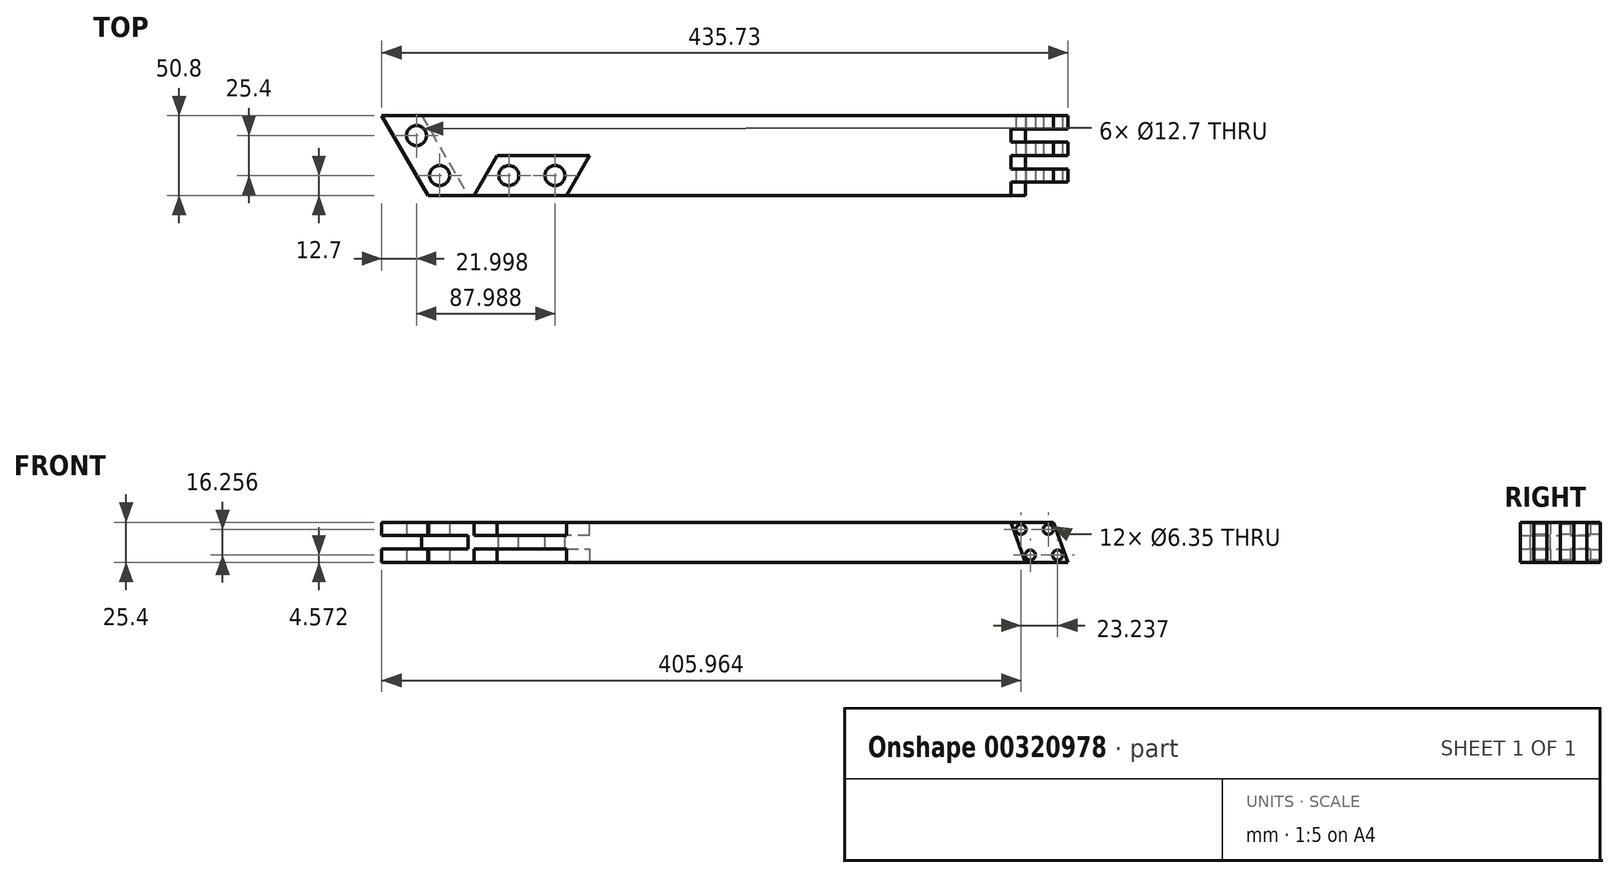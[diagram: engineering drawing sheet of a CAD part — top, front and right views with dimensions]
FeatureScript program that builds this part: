
annotation { "Feature Type Name" : "Feature", "Feature Type Description" : "" }
export const myFeature = defineFeature(function(context is Context, id is Id, definition is map)
    precondition{}
    {
        {
            var Q0;
            Q0=qCreatedBy(makeId("Top.planeOp"),FACE);
            var sketch = newSketch(context, id + "F0", { "sketchPlane" : qUnion([Q0])});
            skLineSegment(sketch, "E0", {"start": v(-203.2, -25.4) * mm, "end": v(-232.53, 25.4) * mm});
            skLineSegment(sketch, "E1", {"start": v(-232.53, 25.4) * mm, "end": v(203.2, 25.4) * mm});
            skLineSegment(sketch, "E2", {"start": v(203.2, 25.4) * mm, "end": v(203.2, -25.4) * mm});
            skLineSegment(sketch, "E3", {"start": v(203.2, -25.4) * mm, "end": v(-203.2, -25.4) * mm});
            skSolve(sketch);
        }
        {
            var Q0;
            Q0=makeQuery(id+"F0.imprint","IMPRINT",FACE,{"disambiguationData":[TD([[makeQuery(id+"F0.imprint","IMPRINT",EDGE,{"derivedFrom":sQuery(id+"F0.wireOp",EDGE,"E0")}),-1.0]])]});
            extrude(context, id + "F1", {"entities" : qUnion([Q0]), "depth" : 25.4 * mm});
        }
        {
            var Q0;
            Q0=makeQuery(id+"F1.opExtrude","CAP_FACE",FACE,{"disambiguationData":[OSD([sQuery(id+"F0.wireOp",EDGE,"E0"),sQuery(id+"F0.wireOp",EDGE,"E1"),sQuery(id+"F0.wireOp",EDGE,"E2"),sQuery(id+"F0.wireOp",EDGE,"E3")])],"isStart":false});
            var sketch = newSketch(context, id + "F2", { "sketchPlane" : qUnion([Q0])});
            skLineSegment(sketch, "E4", {"start": v(-173.87, -25.4) * mm, "end": v(-159.2, 0) * mm});
            skLineSegment(sketch, "E5", {"start": v(-159.2, 0) * mm, "end": v(-100.55, 0) * mm});
            skLineSegment(sketch, "E6", {"start": v(-100.55, 0) * mm, "end": v(-115.21, -25.4) * mm});
            skLineSegment(sketch, "E7", {"start": v(-115.21, -25.4) * mm, "end": v(-173.87, -25.4) * mm});
            skLineSegment(sketch, "E8", {"start": v(-203.2, 25.4) * mm, "end": v(-173.87, -25.4) * mm, "construction": true});
            skSolve(sketch);
        }
        {
            var Q0;
            Q0=makeQuery(id+"F2.imprint","IMPRINT",FACE,{"disambiguationData":[TD([[makeQuery(id+"F2.imprint","IMPRINT",EDGE,{"derivedFrom":sQuery(id+"F2.wireOp",EDGE,"E4")}),-1.0]])]});
            extrude(context, id + "F3", {"entities" : qUnion([Q0]), "operationType" : NewBodyOperationType.REMOVE, "oppositeDirection" : true, "depth" : 8.47 * mm});
        }
        {
            var Q0;
            Q0=makeQuery(id+"F1.opExtrude","CAP_FACE",FACE,{"disambiguationData":[OSD([sQuery(id+"F0.wireOp",EDGE,"E0"),sQuery(id+"F0.wireOp",EDGE,"E1"),sQuery(id+"F0.wireOp",EDGE,"E2"),sQuery(id+"F0.wireOp",EDGE,"E3")])],"isStart":true});
            var sketch = newSketch(context, id + "F4", { "sketchPlane" : qUnion([Q0])});
            skLineSegment(sketch, "E9.0.0", {"start": v(-115.21, 25.4) * mm, "end": v(-100.55, 0) * mm});
            skLineSegment(sketch, "E9.0.1", {"start": v(-100.55, 0) * mm, "end": v(-159.2, 0) * mm});
            skLineSegment(sketch, "E9.0.2", {"start": v(-159.2, 0) * mm, "end": v(-173.87, 25.4) * mm});
            skLineSegment(sketch, "E9.0.3", {"start": v(-173.87, 25.4) * mm, "end": v(-115.21, 25.4) * mm});
            skSolve(sketch);
        }
        {
            var Q0;
            Q0=makeQuery(id+"F4.imprint","IMPRINT",FACE,{"disambiguationData":[TD([[makeQuery(id+"F4.imprint","IMPRINT",EDGE,{"derivedFrom":sQuery(id+"F4.wireOp",EDGE,"E9.0.0")}),-1.0]])]});
            extrude(context, id + "F5", {"entities" : qUnion([Q0]), "operationType" : NewBodyOperationType.REMOVE, "oppositeDirection" : true, "depth" : 8.47 * mm});
        }
        {
            var Q0;
            Q0=makeQuery(id+"F1.opExtrude","SWEPT_FACE",FACE,{"disambiguationData":[OSD([sQuery(id+"F0.wireOp",EDGE,"E1")])]});
            var sketch = newSketch(context, id + "F6", { "sketchPlane" : qUnion([Q0])});
            skLineSegment(sketch, "E10.bottom", {"start": v(232.53, 16.93) * mm, "end": v(207.13, 16.93) * mm});
            skLineSegment(sketch, "E10.top", {"start": v(232.53, 8.47) * mm, "end": v(207.13, 8.47) * mm});
            skLineSegment(sketch, "E10.left", {"start": v(232.53, 16.93) * mm, "end": v(232.53, 8.47) * mm});
            skLineSegment(sketch, "E10.right", {"start": v(207.13, 16.93) * mm, "end": v(207.13, 8.47) * mm});
            skSolve(sketch);
        }
        {
            var Q0;
            Q0=makeQuery(id+"F6.imprint","IMPRINT",FACE,{"disambiguationData":[TD([[makeQuery(id+"F6.imprint","IMPRINT",EDGE,{"derivedFrom":sQuery(id+"F6.wireOp",EDGE,"E10.bottom")}),1.0]])]});
            var Q1;
            Q1=makeQuery(id+"F1.opExtrude","CAP_EDGE",EDGE,{"disambiguationData":[OSD([sQuery(id+"F0.wireOp",EDGE,"E0")])],"isStart":false});
            sweep(context, id + "F7", {"operationType" : NewBodyOperationType.REMOVE, "profiles" : qUnion([Q0]), "path" : qUnion([Q1])});
        }
        {
            var Q0;
            Q0=makeQuery(id+"F1.opExtrude","SWEPT_FACE",FACE,{"disambiguationData":[OSD([sQuery(id+"F0.wireOp",EDGE,"E3")])]});
            var sketch = newSketch(context, id + "F8", { "sketchPlane" : qUnion([Q0])});
            skLineSegment(sketch, "E11", {"start": v(193.96, 25.4) * mm, "end": v(203.2, 0) * mm});
            skSolve(sketch);
        }
        {
            var Q0;
            Q0=makeQuery(id+"F1.opExtrude","CAP_FACE",FACE,{"disambiguationData":[OSD([sQuery(id+"F0.wireOp",EDGE,"E0"),sQuery(id+"F0.wireOp",EDGE,"E1"),sQuery(id+"F0.wireOp",EDGE,"E2"),sQuery(id+"F0.wireOp",EDGE,"E3")])],"isStart":false});
            var sketch = newSketch(context, id + "F9", { "sketchPlane" : qUnion([Q0])});
            skLineSegment(sketch, "E12", {"start": v(193.96, 25.4) * mm, "end": v(193.96, -25.4) * mm});
            skLineSegment(sketch, "E13", {"start": v(193.96, -25.4) * mm, "end": v(203.2, -25.4) * mm});
            skLineSegment(sketch, "E14", {"start": v(203.2, -25.4) * mm, "end": v(203.2, 25.4) * mm});
            skLineSegment(sketch, "E15", {"start": v(203.2, 25.4) * mm, "end": v(193.96, 25.4) * mm});
            skLineSegment(sketch, "E16", {"start": v(193.96, -16.93) * mm, "end": v(166.9, -16.93) * mm});
            skLineSegment(sketch, "E17", {"start": v(166.9, -16.93) * mm, "end": v(166.9, -25.4) * mm});
            skLineSegment(sketch, "E18", {"start": v(166.9, -25.4) * mm, "end": v(193.96, -25.4) * mm});
            skLineSegment(sketch, "E19", {"start": v(193.96, 0) * mm, "end": v(166.9, 0) * mm});
            skLineSegment(sketch, "E20", {"start": v(166.9, 0) * mm, "end": v(166.9, -8.47) * mm});
            skLineSegment(sketch, "E21", {"start": v(166.9, -8.47) * mm, "end": v(193.96, -8.47) * mm});
            skLineSegment(sketch, "E22", {"start": v(193.96, -8.47) * mm, "end": v(193.96, 0) * mm});
            skLineSegment(sketch, "E23", {"start": v(193.96, 8.47) * mm, "end": v(166.9, 8.47) * mm});
            skLineSegment(sketch, "E24", {"start": v(166.9, 8.47) * mm, "end": v(166.9, 16.93) * mm});
            skLineSegment(sketch, "E25", {"start": v(166.9, 16.93) * mm, "end": v(193.96, 16.93) * mm});
            skLineSegment(sketch, "E26", {"start": v(193.96, 16.93) * mm, "end": v(193.96, 8.47) * mm});
            skLineSegment(sketch, "E27", {"start": v(166.9, 25.4) * mm, "end": v(166.9, 16.93) * mm, "construction": true});
            skLineSegment(sketch, "E28", {"start": v(166.9, 8.47) * mm, "end": v(166.9, 0) * mm, "construction": true});
            skLineSegment(sketch, "E29", {"start": v(166.9, -8.47) * mm, "end": v(166.9, -16.93) * mm, "construction": true});
            skSolve(sketch);
        }
        {
            var Q0;
            {var subQ2=sQuery(id+"F9.wireOp",EDGE,"E16");Q0=makeQuery(id+"F9.imprint","IMPRINT",FACE,{"disambiguationData":[TD([[makeQuery(id+"F9.imprint","IMPRINT",EDGE,{"derivedFrom":subQ2}),1.0]])]});}
            var Q1;
            Q1=makeQuery(id+"F9.imprint","IMPRINT",FACE,{"disambiguationData":[TD([[makeQuery(id+"F9.imprint","IMPRINT",EDGE,{"derivedFrom":sQuery(id+"F9.wireOp",EDGE,"E19")}),1.0]])]});
            var Q2;
            Q2=makeQuery(id+"F9.imprint","IMPRINT",FACE,{"disambiguationData":[TD([[makeQuery(id+"F9.imprint","IMPRINT",EDGE,{"derivedFrom":sQuery(id+"F9.wireOp",EDGE,"E23")}),-1.0]])]});
            var Q3;
            {var subQ0=sQuery(id+"F9.wireOp",EDGE,"E13");Q3=makeQuery(id+"F9.imprint","IMPRINT",FACE,{"disambiguationData":[TD([[makeQuery(id+"F9.imprint","IMPRINT",EDGE,{"derivedFrom":subQ0}),-1.0]])]});}
            var Q4;
            Q4=sQuery(id+"F8.wireOp",EDGE,"E11");
            sweep(context, id + "F10", {"operationType" : NewBodyOperationType.REMOVE, "profiles" : qUnion([Q0, Q1, Q2, Q3]), "path" : qUnion([Q4])});
        }
        {
            var Q0;
            Q0=makeQuery(id+"F1.opExtrude","CAP_FACE",FACE,{"disambiguationData":[OSD([sQuery(id+"F0.wireOp",EDGE,"E0"),sQuery(id+"F0.wireOp",EDGE,"E1"),sQuery(id+"F0.wireOp",EDGE,"E2"),sQuery(id+"F0.wireOp",EDGE,"E3")])],"isStart":false});
            var sketch = newSketch(context, id + "F11", { "sketchPlane" : qUnion([Q0])});
            skLineSegment(sketch, "E30.0", {"start": v(-100.55, 0) * mm, "end": v(-115.21, -25.4) * mm});
            skPoint(sketch, "E31.0", {"position": v(-232.53, 25.4) * mm});
            skSolve(sketch);
        }
        {
            var Q0;
            Q0=makeQuery(id+"F10.boolean.opBoolean","COPY",FACE,{"derivedFrom":makeQuery(id+"F10.opSweep","SWEPT_FACE",FACE,{"disambiguationData":[OSD([sQuery(id+"F8.wireOp",EDGE,"E11"),sQuery(id+"F9.wireOp",EDGE,"E16")])]})});
            var sketch = newSketch(context, id + "F12", { "sketchPlane" : qUnion([Q0])});
            skCircle(sketch, "E32", {"center": v(190.75, 20.83) * mm, "radius": 3.18 * mm});
            skCircle(sketch, "E33", {"center": v(173.43, 20.83) * mm, "radius": 3.18 * mm});
            skCircle(sketch, "E34", {"center": v(179.35, 4.57) * mm, "radius": 3.18 * mm});
            skCircle(sketch, "E35", {"center": v(196.67, 4.57) * mm, "radius": 3.18 * mm});
            skLineSegment(sketch, "E36", {"start": v(173.43, 20.83) * mm, "end": v(190.75, 20.83) * mm, "construction": true});
            skLineSegment(sketch, "E37", {"start": v(196.67, 4.57) * mm, "end": v(190.75, 20.83) * mm, "construction": true});
            skLineSegment(sketch, "E38", {"start": v(196.67, 4.57) * mm, "end": v(179.35, 4.57) * mm, "construction": true});
            skLineSegment(sketch, "E39", {"start": v(173.43, 20.83) * mm, "end": v(179.35, 4.57) * mm, "construction": true});
            skSolve(sketch);
        }
        {
            var Q0;
            Q0=makeQuery(id+"F3.boolean.opBoolean","COPY",FACE,{"derivedFrom":makeQuery(id+"F3.opExtrude","CAP_FACE",FACE,{"disambiguationData":[OSD([sQuery(id+"F2.wireOp",EDGE,"E4"),sQuery(id+"F2.wireOp",EDGE,"E5"),sQuery(id+"F2.wireOp",EDGE,"E6"),sQuery(id+"F2.wireOp",EDGE,"E7")])],"isStart":false})});
            var sketch = newSketch(context, id + "F13", { "sketchPlane" : qUnion([Q0])});
            skLineSegment(sketch, "E40", {"start": v(-166.54, -12.7) * mm, "end": v(-107.88, -12.7) * mm, "construction": true});
            skCircle(sketch, "E41", {"center": v(-151.87, -12.7) * mm, "radius": 6.35 * mm});
            skCircle(sketch, "E42", {"center": v(-122.54, -12.7) * mm, "radius": 6.35 * mm});
            skLineSegment(sketch, "E43", {"start": v(-115.21, 0) * mm, "end": v(-129.88, -25.4) * mm, "construction": true});
            skLineSegment(sketch, "E44", {"start": v(-144.54, 0) * mm, "end": v(-159.2, -25.4) * mm, "construction": true});
            skSolve(sketch);
        }
        {
            var Q0;
            Q0=makeQuery(id+"F13.imprint","IMPRINT",FACE,{"disambiguationData":[TD([[makeQuery(id+"F13.imprint","IMPRINT",EDGE,{"derivedFrom":sQuery(id+"F13.wireOp",EDGE,"E41")}),1.0]])]});
            var Q1;
            Q1=makeQuery(id+"F13.imprint","IMPRINT",FACE,{"disambiguationData":[TD([[makeQuery(id+"F13.imprint","IMPRINT",EDGE,{"derivedFrom":sQuery(id+"F13.wireOp",EDGE,"E42")}),1.0]])]});
            extrude(context, id + "F14", {"entities" : qUnion([Q0, Q1]), "operationType" : NewBodyOperationType.REMOVE, "endBound" : BoundingType.THROUGH_ALL, "oppositeDirection" : true, "depth" : 25.4 * mm});
        }
        {
            var Q0;
            Q0=makeQuery(id+"F12.imprint","IMPRINT",FACE,{"disambiguationData":[TD([[makeQuery(id+"F12.imprint","IMPRINT",EDGE,{"derivedFrom":sQuery(id+"F12.wireOp",EDGE,"E32")}),1.0]])]});
            var Q1;
            Q1=makeQuery(id+"F12.imprint","IMPRINT",FACE,{"disambiguationData":[TD([[makeQuery(id+"F12.imprint","IMPRINT",EDGE,{"derivedFrom":sQuery(id+"F12.wireOp",EDGE,"E35")}),1.0]])]});
            var Q2;
            Q2=makeQuery(id+"F12.imprint","IMPRINT",FACE,{"disambiguationData":[TD([[makeQuery(id+"F12.imprint","IMPRINT",EDGE,{"derivedFrom":sQuery(id+"F12.wireOp",EDGE,"E33")}),1.0]])]});
            var Q3;
            Q3=makeQuery(id+"F12.imprint","IMPRINT",FACE,{"disambiguationData":[TD([[makeQuery(id+"F12.imprint","IMPRINT",EDGE,{"derivedFrom":sQuery(id+"F12.wireOp",EDGE,"E34")}),1.0]])]});
            extrude(context, id + "F15", {"entities" : qUnion([Q0, Q1, Q2, Q3]), "operationType" : NewBodyOperationType.REMOVE, "endBound" : BoundingType.THROUGH_ALL, "oppositeDirection" : true, "depth" : 25.4 * mm});
        }
        {
            var Q0;
            Q0=makeQuery(id+"F1.opExtrude","CAP_FACE",FACE,{"disambiguationData":[OSD([sQuery(id+"F0.wireOp",EDGE,"E0"),sQuery(id+"F0.wireOp",EDGE,"E1"),sQuery(id+"F0.wireOp",EDGE,"E2"),sQuery(id+"F0.wireOp",EDGE,"E3")])],"isStart":true});
            var sketch = newSketch(context, id + "F16", { "sketchPlane" : qUnion([Q0])});
            skLineSegment(sketch, "E45", {"start": v(-188.54, 25.4) * mm, "end": v(-217.86, -25.4) * mm, "construction": true});
            skLineSegment(sketch, "E46", {"start": v(-225.2, -12.7) * mm, "end": v(-179.74, -12.7) * mm, "construction": true});
            skLineSegment(sketch, "E47", {"start": v(-210.53, 12.7) * mm, "end": v(-174.67, 12.7) * mm, "construction": true});
            skCircle(sketch, "E48", {"center": v(-195.87, 12.7) * mm, "radius": 6.35 * mm});
            skCircle(sketch, "E49", {"center": v(-210.53, -12.7) * mm, "radius": 6.35 * mm});
            skSolve(sketch);
        }
        {
            var Q0;
            Q0=makeQuery(id+"F16.imprint","IMPRINT",FACE,{"disambiguationData":[TD([[makeQuery(id+"F16.imprint","IMPRINT",EDGE,{"derivedFrom":sQuery(id+"F16.wireOp",EDGE,"E48")}),1.0]])]});
            var Q1;
            Q1=makeQuery(id+"F16.imprint","IMPRINT",FACE,{"disambiguationData":[TD([[makeQuery(id+"F16.imprint","IMPRINT",EDGE,{"derivedFrom":sQuery(id+"F16.wireOp",EDGE,"E49")}),1.0]])]});
            extrude(context, id + "F17", {"entities" : qUnion([Q0, Q1]), "operationType" : NewBodyOperationType.REMOVE, "endBound" : BoundingType.THROUGH_ALL, "oppositeDirection" : true, "depth" : 25.4 * mm});
        }
    });
